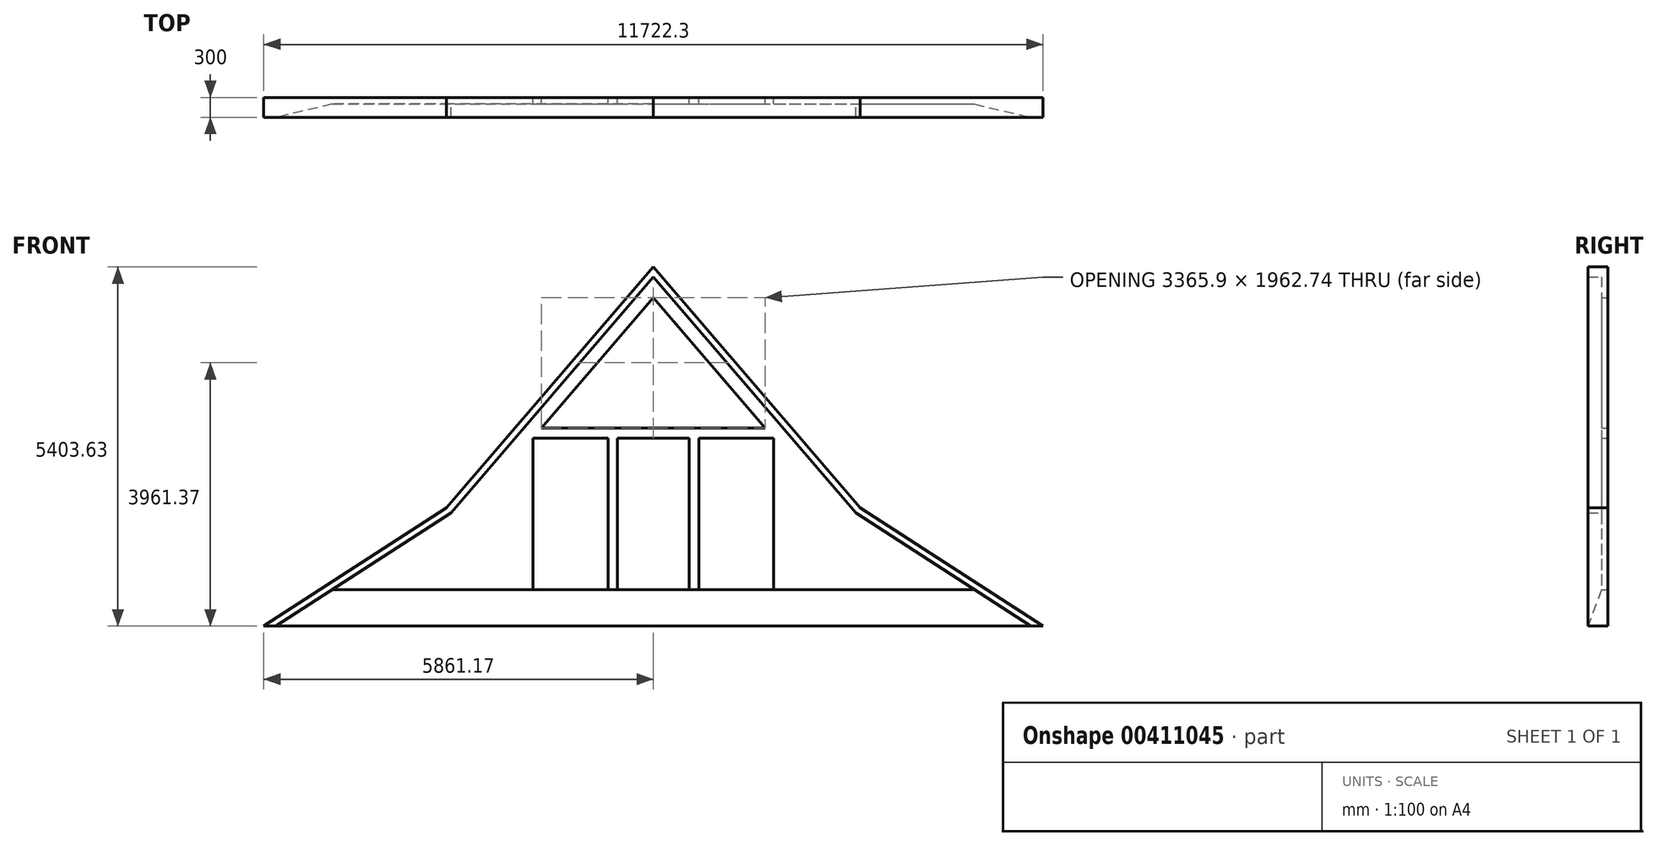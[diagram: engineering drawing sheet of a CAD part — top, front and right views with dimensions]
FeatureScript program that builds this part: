
annotation { "Feature Type Name" : "Feature", "Feature Type Description" : "" }
export const myFeature = defineFeature(function(context is Context, id is Id, definition is map)
    precondition{}
    {
        {
            var Q0;
            Q0=qCreatedBy(makeId("Front.planeOp"),FACE);
            var sketch = newSketch(context, id + "F0", { "sketchPlane" : qUnion([Q0])});
            skLineSegment(sketch, "E0", {"start": v(-4030, 0) * mm, "end": v(4030, 0) * mm});
            skLineSegment(sketch, "E1", {"start": v(0, 0) * mm, "end": v(0, 4700) * mm, "construction": true});
            skLineSegment(sketch, "E2", {"start": v(0, 4700) * mm, "end": v(-3043.94, 1150) * mm});
            skLineSegment(sketch, "E3", {"start": v(0, 4700) * mm, "end": v(3043.94, 1150) * mm});
            skPoint(sketch, "E4", {"position": v(3043.94, 1150) * mm});
            skLineSegment(sketch, "E5", {"start": v(-4825, 0) * mm, "end": v(4825, 0) * mm});
            skLineSegment(sketch, "E6", {"start": v(3043.94, 1150) * mm, "end": v(4825, 0) * mm});
            skLineSegment(sketch, "E7", {"start": v(-3043.94, 1150) * mm, "end": v(-4825, 0) * mm});
            skLineSegment(sketch, "E8", {"start": v(-4825, 0) * mm, "end": v(-5676.81, -550) * mm});
            skLineSegment(sketch, "E9", {"start": v(-5676.81, -550) * mm, "end": v(5676.81, -550) * mm});
            skLineSegment(sketch, "E10", {"start": v(5676.81, -550) * mm, "end": v(4825, 0) * mm});
            skLineSegment(sketch, "E11", {"start": v(-1811.57, 0) * mm, "end": v(1811.57, 0) * mm});
            skLineSegment(sketch, "E12", {"start": v(-1811.57, 0) * mm, "end": v(-1811.57, 2280) * mm});
            skLineSegment(sketch, "E13", {"start": v(-1811.57, 2280) * mm, "end": v(1811.57, 2280) * mm});
            skLineSegment(sketch, "E14", {"start": v(1811.57, 2280) * mm, "end": v(1811.57, 0) * mm});
            skLineSegment(sketch, "E15", {"start": v(-681.57, 2280) * mm, "end": v(-681.57, 0) * mm});
            skLineSegment(sketch, "E16", {"start": v(-541.57, 0) * mm, "end": v(-541.57, 2280) * mm});
            skLineSegment(sketch, "E17", {"start": v(541.57, 2280) * mm, "end": v(541.57, 0) * mm});
            skLineSegment(sketch, "E18", {"start": v(681.57, 0) * mm, "end": v(681.57, 2280) * mm});
            skLineSegment(sketch, "E19", {"start": v(-1682.95, 2430) * mm, "end": v(1682.95, 2430) * mm});
            skPoint(sketch, "E20", {"position": v(0, 2430) * mm});
            skLineSegment(sketch, "E21", {"start": v(0, 2430) * mm, "end": v(0, 4392.74) * mm, "construction": true});
            skLineSegment(sketch, "E22", {"start": v(0, 4392.74) * mm, "end": v(-1682.95, 2430) * mm});
            skLineSegment(sketch, "E23", {"start": v(0, 4392.74) * mm, "end": v(1682.95, 2430) * mm});
            skLineSegment(sketch, "E24", {"start": v(1682.95, 2430) * mm, "end": v(1811.57, 2280) * mm, "construction": true});
            skLineSegment(sketch, "E25", {"start": v(-1682.95, 2430) * mm, "end": v(-1811.57, 2280) * mm, "construction": true});
            skSolve(sketch);
        }
        {
            var Q0;
            Q0=makeQuery(id+"F0.imprint","IMPRINT",FACE,{"disambiguationData":[TD([[makeQuery(id+"F0.imprint","IMPRINT",EDGE,{"derivedFrom":sQuery(id+"F0.wireOp",EDGE,"E2")}),1.0]])]});
            var Q1;
            {var subQ0=sQuery(id+"F0.wireOp",EDGE,"E15");Q1=makeQuery(id+"F0.imprint","IMPRINT",FACE,{"disambiguationData":[TD([[makeQuery(id+"F0.imprint","IMPRINT",EDGE,{"derivedFrom":subQ0}),1.0]])]});}
            var Q2;
            {var subQ0=sQuery(id+"F0.wireOp",EDGE,"E17");Q2=makeQuery(id+"F0.imprint","IMPRINT",FACE,{"disambiguationData":[TD([[makeQuery(id+"F0.imprint","IMPRINT",EDGE,{"derivedFrom":subQ0}),1.0]])]});}
            extrude(context, id + "F1", {"entities" : qUnion([Q0, Q1, Q2]), "depth" : 100 * mm});
        }
        {
            var Q0;
            {var subQ6=sQuery(id+"F0.wireOp",EDGE,"E8");Q0=makeQuery(id+"F0.imprint","IMPRINT",FACE,{"disambiguationData":[TD([[makeQuery(id+"F0.imprint","IMPRINT",EDGE,{"derivedFrom":subQ6}),1.0]])]});}
            extrude(context, id + "F2", {"entities" : qUnion([Q0]), "operationType" : NewBodyOperationType.ADD, "depth" : 300 * mm});
        }
        {
            var Q0;
            Q0=qCreatedBy(makeId("Right.planeOp"),FACE);
            var sketch = newSketch(context, id + "F3", { "sketchPlane" : qUnion([Q0])});
            skLineSegment(sketch, "E26.0", {"start": v(-300, 0) * mm, "end": v(-100, 0) * mm});
            skLineSegment(sketch, "E27.0", {"start": v(-300, 0) * mm, "end": v(-300, -550) * mm});
            skLineSegment(sketch, "E28", {"start": v(-100, 0) * mm, "end": v(-300, -550) * mm});
            skSolve(sketch);
        }
        {
            var Q0;
            Q0 = qSketchRegion(id + "F3", true);
            extrude(context, id + "F4", {"entities" : qUnion([Q0]), "operationType" : NewBodyOperationType.REMOVE, "endBound" : BoundingType.SYMMETRIC, "oppositeDirection" : true, "depth" : 13000 * mm});
        }
        {
            var Q0;
            Q0=qCreatedBy(makeId("Front.planeOp"),FACE);
            var sketch = newSketch(context, id + "F5", { "sketchPlane" : qUnion([Q0])});
            skLineSegment(sketch, "E29.0", {"start": v(0, 4700) * mm, "end": v(-3043.94, 1150) * mm});
            skLineSegment(sketch, "E30.0", {"start": v(-3043.94, 1150) * mm, "end": v(-4825, 0) * mm});
            skLineSegment(sketch, "E31.0", {"start": v(-4825, 0) * mm, "end": v(-5676.81, -550) * mm});
            skLineSegment(sketch, "E32.0", {"start": v(0, 4700) * mm, "end": v(3043.94, 1150) * mm});
            skLineSegment(sketch, "E33.0", {"start": v(3043.94, 1150) * mm, "end": v(4825, 0) * mm});
            skLineSegment(sketch, "E34.0", {"start": v(5676.81, -550) * mm, "end": v(4825, 0) * mm});
            skLineSegment(sketch, "E35.0", {"start": v(-4879.24, 84) * mm, "end": v(-5730.85, -465.85) * mm});
            skLineSegment(sketch, "E35.1", {"start": v(-3110.39, 1226.13) * mm, "end": v(-4879.24, 84) * mm});
            skLineSegment(sketch, "E35.2", {"start": v(-75.91, 4765.1) * mm, "end": v(-3110.39, 1226.13) * mm});
            skLineSegment(sketch, "E36.0", {"start": v(5731.06, -466) * mm, "end": v(4879.24, 84) * mm});
            skLineSegment(sketch, "E36.1", {"start": v(3110.39, 1226.13) * mm, "end": v(4879.24, 84) * mm});
            skLineSegment(sketch, "E36.2", {"start": v(75.94, 4765.06) * mm, "end": v(3110.39, 1226.13) * mm});
            skLineSegment(sketch, "E37", {"start": v(-75.91, 4765.1) * mm, "end": v(0, 4853.63) * mm});
            skLineSegment(sketch, "E38", {"start": v(0, 4853.63) * mm, "end": v(75.94, 4765.06) * mm});
            skLineSegment(sketch, "E39", {"start": v(-5730.85, -465.85) * mm, "end": v(-5861.17, -550) * mm});
            skLineSegment(sketch, "E40", {"start": v(-5861.17, -550) * mm, "end": v(-5676.81, -550) * mm});
            skLineSegment(sketch, "E41", {"start": v(5731.06, -466) * mm, "end": v(5861.17, -550) * mm});
            skLineSegment(sketch, "E42", {"start": v(5861.17, -550) * mm, "end": v(5676.81, -550) * mm});
            skSolve(sketch);
        }
        {
            var Q0;
            Q0 = qSketchRegion(id + "F5", true);
            extrude(context, id + "F6", {"entities" : qUnion([Q0]), "operationType" : NewBodyOperationType.ADD, "depth" : 300 * mm});
        }
    });
